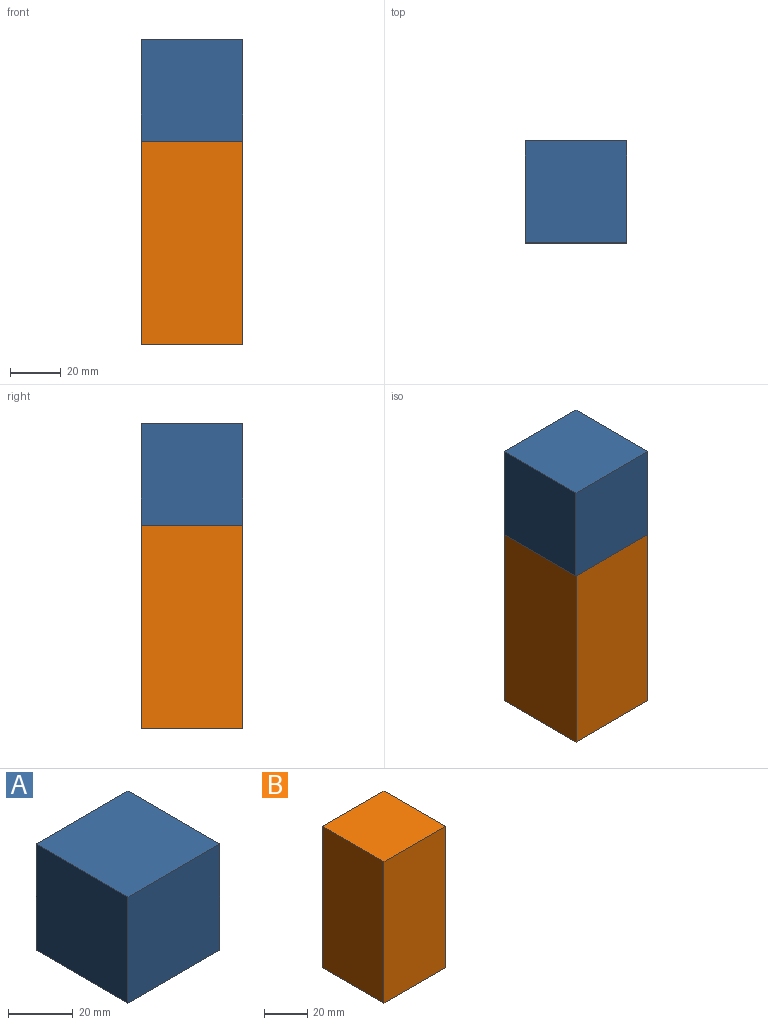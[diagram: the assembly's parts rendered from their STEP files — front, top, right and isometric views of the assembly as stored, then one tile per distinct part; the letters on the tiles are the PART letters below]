
ASSEMBLY  parts=2 mates=1
PART A: 6 faces, bbox 40x40x40 mm
  f0: plane 40x40mm, normal (1,0,0), area 1600mm2, adj f1,f3,f4,f5
  f1: plane 40x40mm, normal (0,0,1), area 1600mm2, adj f0,f2,f4,f5
  f2: plane 40x40mm, normal (-1,0,0), area 1600mm2, adj f1,f3,f4,f5
  f3: plane 40x40mm, normal (0,0,-1), area 1600mm2, adj f0,f2,f4,f5
  f4: plane 40x40mm, normal (0,1,0), area 1600mm2, adj f0,f1,f2,f3
  f5: plane 40x40mm, normal (0,-1,0), area 1600mm2, adj f0,f1,f2,f3
PART B: 6 faces, bbox 40x40x80 mm
  f0: plane 40x40mm, normal (0,0,1), area 1600mm2, adj f1,f3,f4,f5
  f1: plane 80x40mm, normal (-1,0,0), area 3200mm2, adj f0,f2,f4,f5
  f2: plane 40x40mm, normal (0,0,-1), area 1600mm2, adj f1,f3,f4,f5
  f3: plane 80x40mm, normal (1,0,0), area 3200mm2, adj f0,f2,f4,f5
  f4: plane 80x40mm, normal (0,-1,0), area 3200mm2, adj f0,f1,f2,f3
  f5: plane 80x40mm, normal (0,1,0), area 3200mm2, adj f0,f1,f2,f3
PLACE A rot(axis=(-1,0,0),90deg) t=(442.77,978.64,-198.85)mm
PLACE B t=(329.6,978.64,-258.85)mm
MATE fastened A.f4 <-> B.f0  axis (0,0,-1) through (422.77,998.64,-218.85)mm
